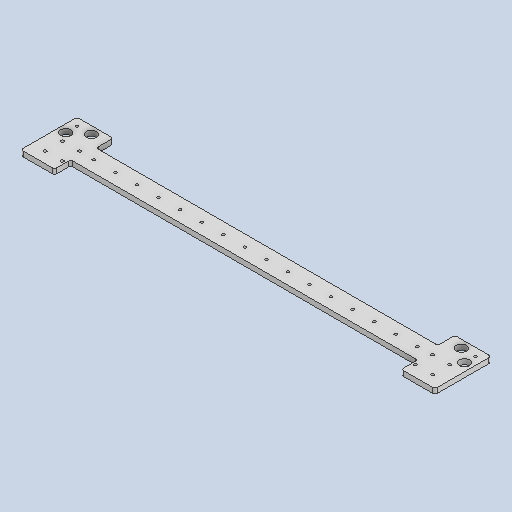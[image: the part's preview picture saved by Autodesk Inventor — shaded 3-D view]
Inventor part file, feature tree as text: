
AUTODESK INVENTOR PART (.ipt)
format: ipt  version: 2024.2 (Build 282272000, 272)  size: 129,024 bytes
history: native  units: in
note: dims shown in document units (in); Inventor stores cm internally (conversion verified against a paired STEP export)
features: fillet x1
ambient origin geometry x8: Origin, YZ Plane, XZ Plane, XY Plane, X Axis, Y Axis, Z Axis, Center Point
bodies: Solid1 (feature_tree)
feature tree (1):
  fillet  "Fillet1"  [1 undecoded]
note: 1 required parameter value undecoded (feature->parameter linkage not recoverable at this tier; creation-order binding heuristic only, values carry confidence <= 0.55)
